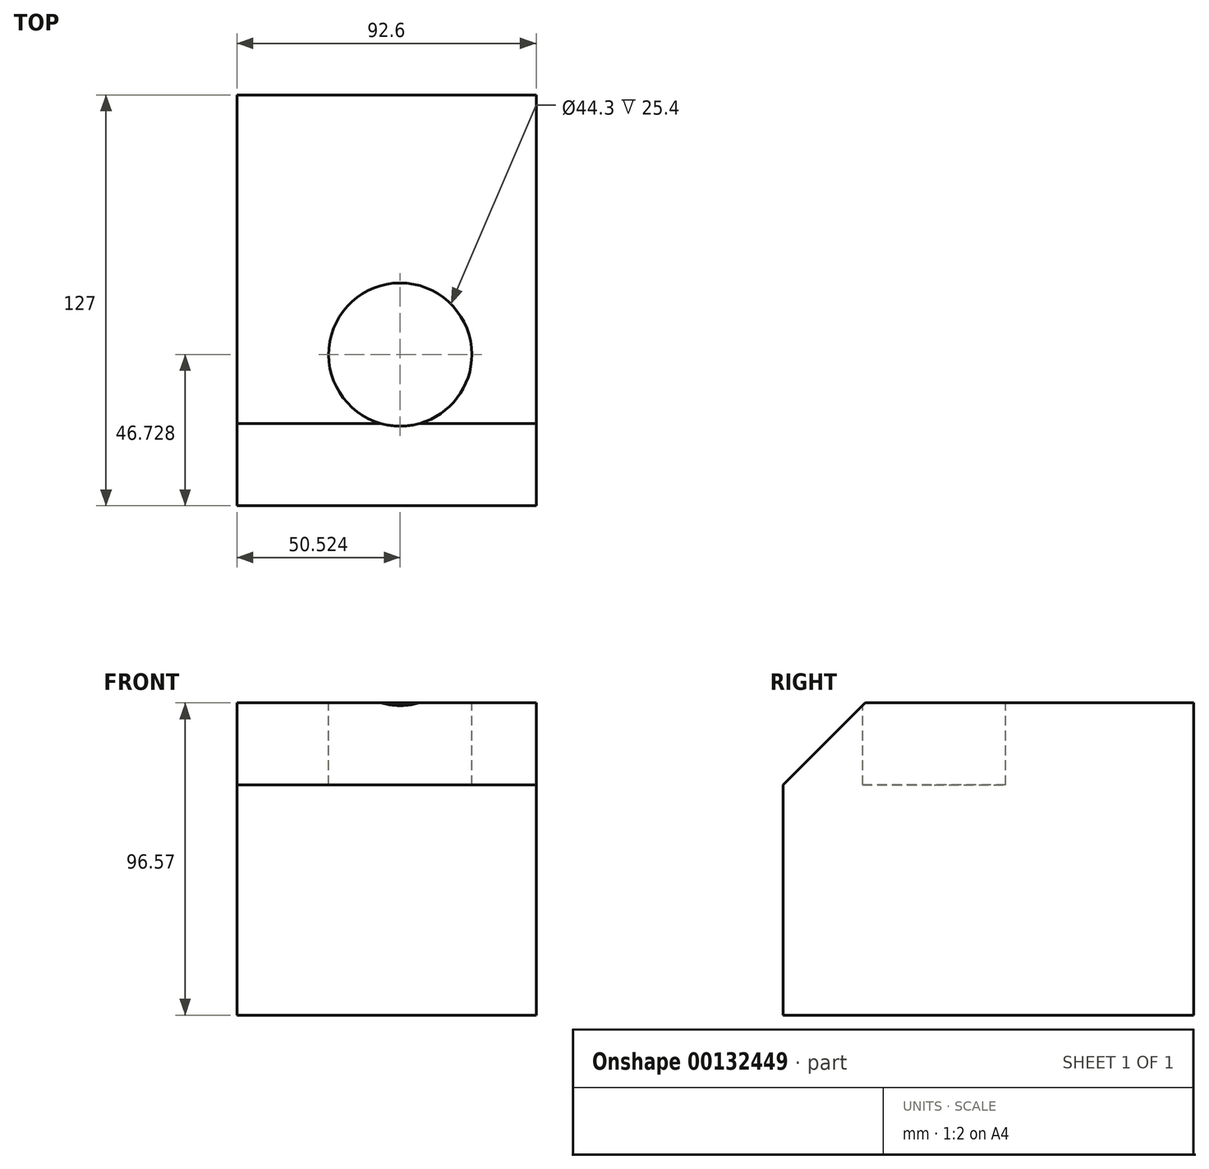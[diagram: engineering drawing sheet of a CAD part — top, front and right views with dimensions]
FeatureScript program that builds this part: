
annotation { "Feature Type Name" : "Feature", "Feature Type Description" : "" }
export const myFeature = defineFeature(function(context is Context, id is Id, definition is map)
    precondition{}
    {
        {
            var Q0;
            Q0=qCreatedBy(makeId("Front.planeOp"),FACE);
            var sketch = newSketch(context, id + "F0", { "sketchPlane" : qUnion([Q0])});
            skLineSegment(sketch, "E0.bottom", {"start": v(-46, 47.69) * mm, "end": v(46.6, 47.69) * mm});
            skLineSegment(sketch, "E0.top", {"start": v(-46, -48.88) * mm, "end": v(46.6, -48.88) * mm});
            skLineSegment(sketch, "E0.left", {"start": v(-46, 47.69) * mm, "end": v(-46, -48.88) * mm});
            skLineSegment(sketch, "E0.right", {"start": v(46.6, 47.69) * mm, "end": v(46.6, -48.88) * mm});
            skSolve(sketch);
        }
        {
            var Q0;
            Q0=makeQuery(id+"F0.imprint","IMPRINT",FACE,{"disambiguationData":[TD([[makeQuery(id+"F0.imprint","IMPRINT",EDGE,{"derivedFrom":sQuery(id+"F0.wireOp",EDGE,"E0.bottom")}),-1.0]])]});
            extrude(context, id + "F1", {"entities" : qUnion([Q0]), "depth" : 127 * mm});
        }
        {
            var Q0;
            Q0=makeQuery(id+"F1.opExtrude","SWEPT_FACE",FACE,{"disambiguationData":[OSD([sQuery(id+"F0.wireOp",EDGE,"E0.bottom")])]});
            var sketch = newSketch(context, id + "F2", { "sketchPlane" : qUnion([Q0])});
            skCircle(sketch, "E1", {"center": v(4.52, -80.27) * mm, "radius": 22.15 * mm});
            skSolve(sketch);
        }
        {
            var Q0;
            Q0=makeQuery(id+"F2.imprint","IMPRINT",FACE,{"disambiguationData":[TD([[makeQuery(id+"F2.imprint","IMPRINT",EDGE,{"derivedFrom":sQuery(id+"F2.wireOp",EDGE,"E1")}),1.0]])]});
            extrude(context, id + "F3", {"entities" : qUnion([Q0]), "operationType" : NewBodyOperationType.REMOVE, "oppositeDirection" : true, "depth" : 25.4 * mm});
        }
        {
            var Q0;
            Q0=makeQuery(id+"F1.opExtrude","CAP_EDGE",EDGE,{"disambiguationData":[OSD([sQuery(id+"F0.wireOp",EDGE,"E0.bottom")])],"isStart":false});
            chamfer(context, id + "F4", {"entities" : qUnion([Q0]), "width" : 25.4 * mm, "tangentPropagation" : true});
        }
    });
